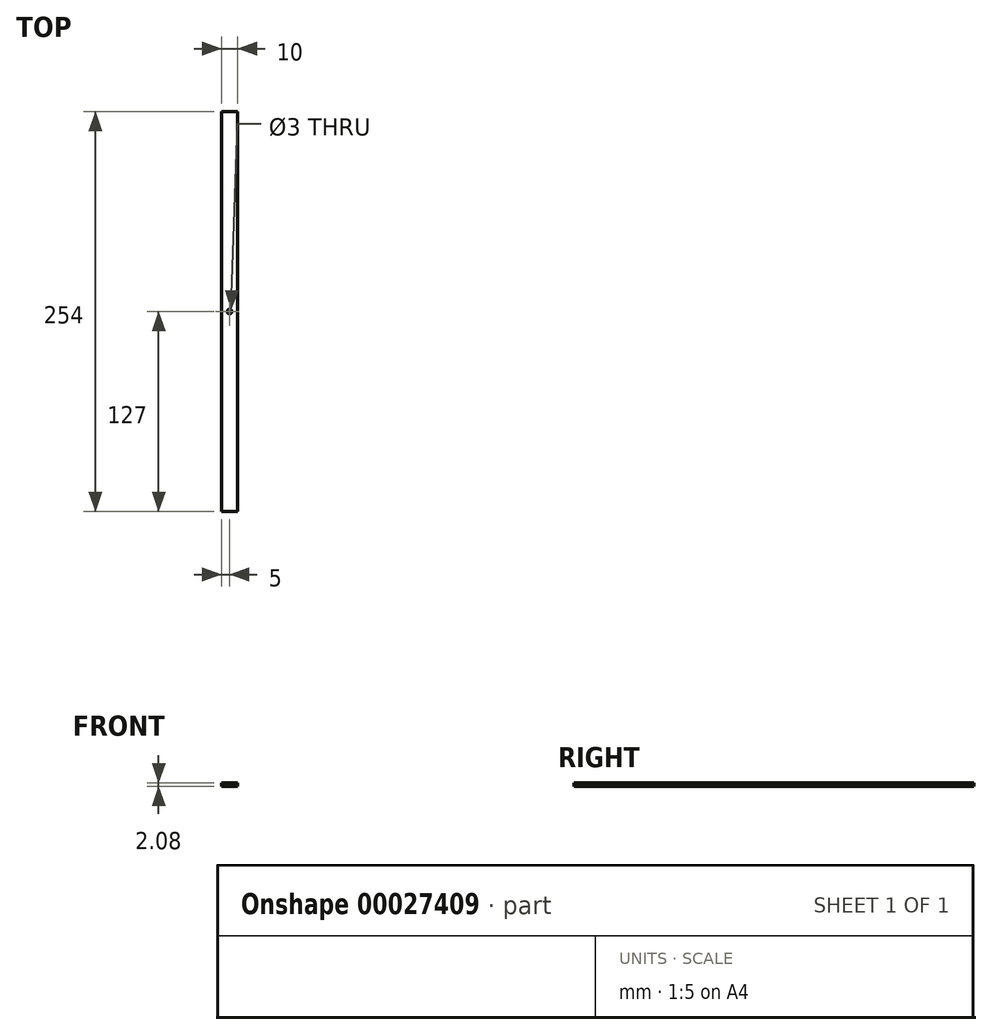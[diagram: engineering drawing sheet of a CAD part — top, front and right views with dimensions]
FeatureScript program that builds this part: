
annotation { "Feature Type Name" : "Feature", "Feature Type Description" : "" }
export const myFeature = defineFeature(function(context is Context, id is Id, definition is map)
    precondition{}
    {
        {
            var Q0;
            Q0=qCreatedBy(makeId("Front.planeOp"),FACE);
            var sketch = newSketch(context, id + "F0", { "sketchPlane" : qUnion([Q0])});
            skLineSegment(sketch, "E0.rect.bottom", {"start": v(5, 1.04) * mm, "end": v(-5, 1.04) * mm});
            skLineSegment(sketch, "E0.rect.top", {"start": v(5, -1.04) * mm, "end": v(-5, -1.04) * mm});
            skLineSegment(sketch, "E0.rect.left", {"start": v(5, 1.04) * mm, "end": v(5, -1.04) * mm});
            skLineSegment(sketch, "E0.rect.right", {"start": v(-5, 1.04) * mm, "end": v(-5, -1.04) * mm});
            skPoint(sketch, "E0.rect.middle", {"position": v(0, 0) * mm});
            skSolve(sketch);
        }
        {
            var Q0;
            Q0=makeQuery(id+"F0.imprint","IMPRINT",FACE,{"disambiguationData":[TD([[makeQuery(id+"F0.imprint","IMPRINT",EDGE,{"derivedFrom":sQuery(id+"F0.wireOp",EDGE,"E0.rect.bottom")}),1.0]])]});
            extrude(context, id + "F1", {"entities" : qUnion([Q0]), "depth" : 127 * mm, "hasSecondDirection" : true, "secondDirectionOppositeDirection" : true, "secondDirectionDepth" : 127 * mm});
        }
        {
            var Q0;
            Q0=makeQuery(id+"F1.opExtrude","SWEPT_FACE",FACE,{"disambiguationData":[OSD([sQuery(id+"F0.wireOp",EDGE,"E0.rect.bottom")])]});
            var sketch = newSketch(context, id + "F2", { "sketchPlane" : qUnion([Q0])});
            skCircle(sketch, "E1", {"center": v(0, 0) * mm, "radius": 1.5 * mm});
            skSolve(sketch);
        }
        {
            var Q0;
            Q0=makeQuery(id+"F2.imprint","IMPRINT",FACE,{"disambiguationData":[TD([[makeQuery(id+"F2.imprint","IMPRINT",EDGE,{"derivedFrom":sQuery(id+"F2.wireOp",EDGE,"E1")}),1.0]])]});
            extrude(context, id + "F3", {"entities" : qUnion([Q0]), "operationType" : NewBodyOperationType.REMOVE, "oppositeDirection" : true, "depth" : 25 * mm});
        }
    });
